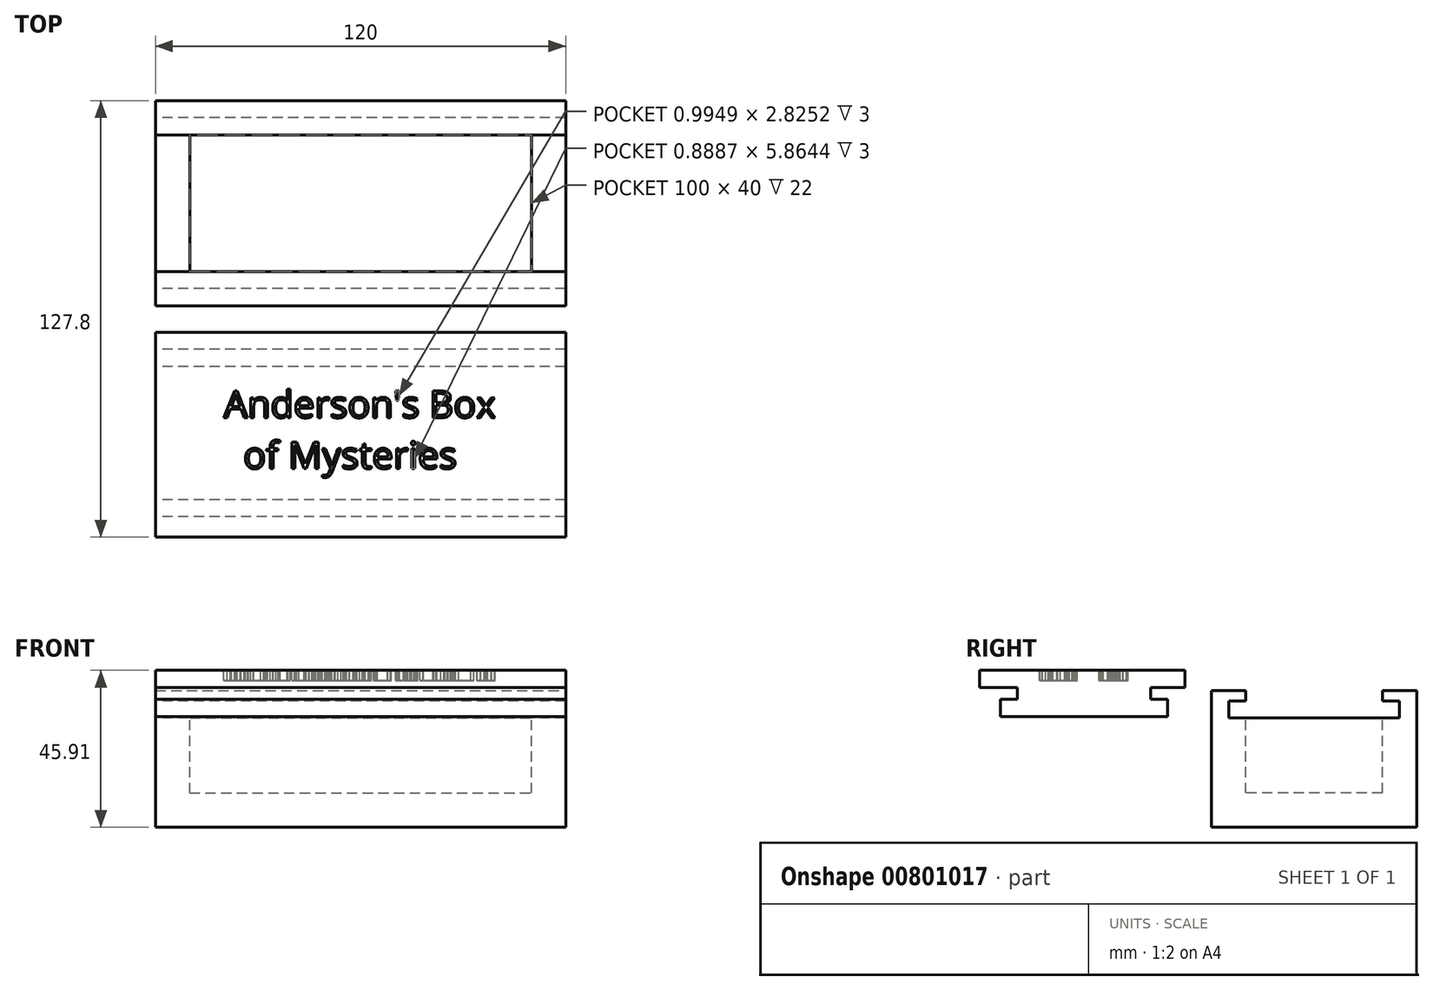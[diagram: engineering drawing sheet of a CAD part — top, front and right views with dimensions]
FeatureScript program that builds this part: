
annotation { "Feature Type Name" : "Feature", "Feature Type Description" : "" }
export const myFeature = defineFeature(function(context is Context, id is Id, definition is map)
    precondition{}
    {
        {
            var Q0;
            Q0=qCreatedBy(makeId("Top.planeOp"),FACE);
            var sketch = newSketch(context, id + "F0", { "sketchPlane" : qUnion([Q0])});
            skLineSegment(sketch, "E0.bottom", {"start": v(0, 0) * mm, "end": v(120, 0) * mm});
            skLineSegment(sketch, "E0.top", {"start": v(0, 60) * mm, "end": v(120, 60) * mm});
            skLineSegment(sketch, "E0.left", {"start": v(0, 0) * mm, "end": v(0, 60) * mm});
            skLineSegment(sketch, "E0.right", {"start": v(120, 0) * mm, "end": v(120, 60) * mm});
            skSolve(sketch);
        }
        {
            var Q0;
            Q0=makeQuery(id+"F0.imprint","IMPRINT",FACE,{"disambiguationData":[TD([[makeQuery(id+"F0.imprint","IMPRINT",EDGE,{"derivedFrom":sQuery(id+"F0.wireOp",EDGE,"E0.bottom")}),1.0]])]});
            extrude(context, id + "F1", {"entities" : qUnion([Q0]), "depth" : 40 * mm, "offsetDistance" : 25 * mm});
        }
        {
            var Q0;
            Q0=makeQuery(id+"F1.opExtrude","CAP_FACE",FACE,{"disambiguationData":[OSD([sQuery(id+"F0.wireOp",EDGE,"E0.bottom"),sQuery(id+"F0.wireOp",EDGE,"E0.top"),sQuery(id+"F0.wireOp",EDGE,"E0.left"),sQuery(id+"F0.wireOp",EDGE,"E0.right")])],"isStart":false});
            var sketch = newSketch(context, id + "F2", { "sketchPlane" : qUnion([Q0])});
            skLineSegment(sketch, "E1.bottom", {"start": v(10, 50) * mm, "end": v(110, 50) * mm});
            skLineSegment(sketch, "E1.top", {"start": v(10, 10) * mm, "end": v(110, 10) * mm});
            skLineSegment(sketch, "E1.left", {"start": v(10, 50) * mm, "end": v(10, 10) * mm});
            skLineSegment(sketch, "E1.right", {"start": v(110, 50) * mm, "end": v(110, 10) * mm});
            skSolve(sketch);
        }
        {
            var Q0;
            Q0=makeQuery(id+"F2.imprint","IMPRINT",FACE,{"disambiguationData":[TD([[makeQuery(id+"F2.imprint","IMPRINT",EDGE,{"derivedFrom":sQuery(id+"F2.wireOp",EDGE,"E1.bottom")}),-1.0]])]});
            extrude(context, id + "F3", {"entities" : qUnion([Q0]), "operationType" : NewBodyOperationType.REMOVE, "oppositeDirection" : true, "depth" : 30 * mm, "offsetDistance" : 25 * mm});
        }
        {
            var Q0;
            Q0=makeQuery(id+"F1.opExtrude","SWEPT_FACE",FACE,{"disambiguationData":[OSD([sQuery(id+"F0.wireOp",EDGE,"E0.left")])]});
            var sketch = newSketch(context, id + "F4", { "sketchPlane" : qUnion([Q0])});
            skLineSegment(sketch, "E2.bottom", {"start": v(-55, 37) * mm, "end": v(-50, 37) * mm});
            skLineSegment(sketch, "E2.top", {"start": v(-55, 32) * mm, "end": v(-5, 32) * mm});
            skLineSegment(sketch, "E2.left", {"start": v(-55, 37) * mm, "end": v(-55, 32) * mm});
            skLineSegment(sketch, "E2.right", {"start": v(-5, 37) * mm, "end": v(-5, 32) * mm});
            skLineSegment(sketch, "E3.top", {"start": v(-50, 40) * mm, "end": v(-10, 40) * mm});
            skLineSegment(sketch, "E3.left", {"start": v(-50, 37) * mm, "end": v(-50, 40) * mm});
            skLineSegment(sketch, "E3.right", {"start": v(-10, 37) * mm, "end": v(-10, 40) * mm});
            skLineSegment(sketch, "E4.trimOffspring", {"start": v(-10, 37) * mm, "end": v(-5, 37) * mm});
            skSolve(sketch);
        }
        {
            var Q0;
            Q0=makeQuery(id+"F4.imprint","IMPRINT",FACE,{"disambiguationData":[TD([[makeQuery(id+"F4.imprint","IMPRINT",EDGE,{"derivedFrom":sQuery(id+"F4.wireOp",EDGE,"E2.bottom")}),-1.0]])]});
            extrude(context, id + "F5", {"entities" : qUnion([Q0]), "operationType" : NewBodyOperationType.REMOVE, "oppositeDirection" : true, "depth" : 120 * mm, "offsetDistance" : 25 * mm});
        }
        {
            var Q0;
            Q0=qCreatedBy(makeId("Right.planeOp"),FACE);
            var sketch = newSketch(context, id + "F6", { "sketchPlane" : qUnion([Q0])});
            skLineSegment(sketch, "E5.bottom", {"start": v(-12.8, 37.4) * mm, "end": v(-17.8, 37.4) * mm});
            skLineSegment(sketch, "E5.top", {"start": v(-12.8, 32.4) * mm, "end": v(-61.8, 32.4) * mm});
            skLineSegment(sketch, "E5.left", {"start": v(-12.8, 37.4) * mm, "end": v(-12.8, 32.4) * mm});
            skLineSegment(sketch, "E5.right", {"start": v(-61.8, 37.4) * mm, "end": v(-61.8, 32.4) * mm});
            skLineSegment(sketch, "E6.left", {"start": v(-17.8, 37.4) * mm, "end": v(-17.8, 40.9) * mm});
            skLineSegment(sketch, "E6.right", {"start": v(-56.8, 37.4) * mm, "end": v(-56.8, 40.9) * mm});
            skLineSegment(sketch, "E7.bottom", {"start": v(-7.8, 40.9) * mm, "end": v(-17.8, 40.9) * mm});
            skLineSegment(sketch, "E7.top", {"start": v(-7.8, 45.9) * mm, "end": v(-67.8, 45.9) * mm});
            skLineSegment(sketch, "E7.left", {"start": v(-7.8, 40.9) * mm, "end": v(-7.8, 45.9) * mm});
            skLineSegment(sketch, "E7.right", {"start": v(-67.8, 40.9) * mm, "end": v(-67.8, 45.9) * mm});
            skLineSegment(sketch, "E8.trimOffspring", {"start": v(-56.8, 40.9) * mm, "end": v(-67.8, 40.9) * mm});
            skLineSegment(sketch, "E9.trimOffspring", {"start": v(-56.8, 37.4) * mm, "end": v(-61.8, 37.4) * mm});
            skSolve(sketch);
        }
        {
            var Q0;
            Q0=makeQuery(id+"F6.imprint","IMPRINT",FACE,{"disambiguationData":[TD([[makeQuery(id+"F6.imprint","IMPRINT",EDGE,{"derivedFrom":sQuery(id+"F6.wireOp",EDGE,"E5.bottom")}),1.0]])]});
            extrude(context, id + "F7", {"entities" : qUnion([Q0]), "depth" : 120 * mm, "offsetDistance" : 25 * mm});
        }
        {
            var Q0;
            Q0=makeQuery(id+"F7.opExtrude","SWEPT_FACE",FACE,{"disambiguationData":[OSD([sQuery(id+"F6.wireOp",EDGE,"E7.top")])]});
            var sketch = newSketch(context, id + "F8", { "sketchPlane" : qUnion([Q0])});
            skText(sketch, "E10", { "text": "Anderson\'s Box\n  of Mysteries", "fontName": "OpenSans-Regular.ttf"});
            const initialGuessF8  = {"E10": [0.02, -0.0328, 1, 0, 0.00789]};
            skSetInitialGuess(sketch, initialGuessF8);
            skSolve(sketch);
        }
        {
            var Q0;
            Q0 = qSketchRegion(id + "F8", true);
            extrude(context, id + "F9", {"entities" : qUnion([Q0]), "operationType" : NewBodyOperationType.REMOVE, "oppositeDirection" : true, "depth" : 3 * mm, "offsetDistance" : 25 * mm});
        }
    });
